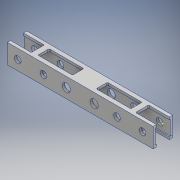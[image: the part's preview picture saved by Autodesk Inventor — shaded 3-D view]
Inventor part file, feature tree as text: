
AUTODESK INVENTOR PART (.ipt)
format: ipt  version: 2017 (Build 210142000, 142)  size: 266,752 bytes
history: native  units: mm
features: sketch x5, extrude x4
ambient origin geometry x8: Origin, YZ Plane, XZ Plane, XY Plane, X Axis, Y Axis, Z Axis, Center Point
bodies: Solid1 (feature_tree)
feature tree (9):
  extrude  "Extrusion1"  Depth=9.525mm TaperAngle=0.0deg
  extrude  "Extrusion2"  Depth=9.525mm TaperAngle=0.0deg
  extrude  "Extrusion3"  Depth=9.525mm TaperAngle=0.0deg
  extrude  "Extrusion5"  Depth=9.525mm TaperAngle=0.0deg
  sketch  "Sketch6"
  sketch  "Sketch1"  dims[d0=135.4mm d1=44.0mm d2=78.105mm d3=50.8mm d4=44.45mm d5=21.59mm d6=135.4mm d7=44.0mm d8=78.105mm d9=50.8mm d10=568.96mm d11=21.59mm d12=9.525mm d13=0.0mm]
  sketch  "Sketch2"  dims[d14=26.0mm d15=26.0mm d16=32.0mm d17=26.0mm d18=26.0mm d19=32.0mm d20=568.96mm d21=57.15mm d22=40.64mm d23=140.776mm d24=230.152mm d25=230.152mm d26=40.64mm d27=140.776mm d28=9.525mm d29=0.0mm]
  sketch  "Sketch3"  dims[d30=26.0mm d31=26.0mm d32=32.0mm d33=26.0mm d34=26.0mm d35=32.0mm d36=568.96mm d37=57.15mm d38=40.64mm d39=140.776mm d40=230.152mm d41=230.152mm d42=40.64mm d43=140.776mm d44=9.525mm d45=0.0mm]
  sketch  "Sketch5"  dims[d60=135.4mm d61=44.0mm d62=78.105mm d63=50.8mm d64=44.45mm d65=21.59mm d66=135.4mm d67=44.0mm d68=78.105mm d69=50.8mm d70=568.96mm d71=21.59mm d72=9.525mm d73=0.0mm]
